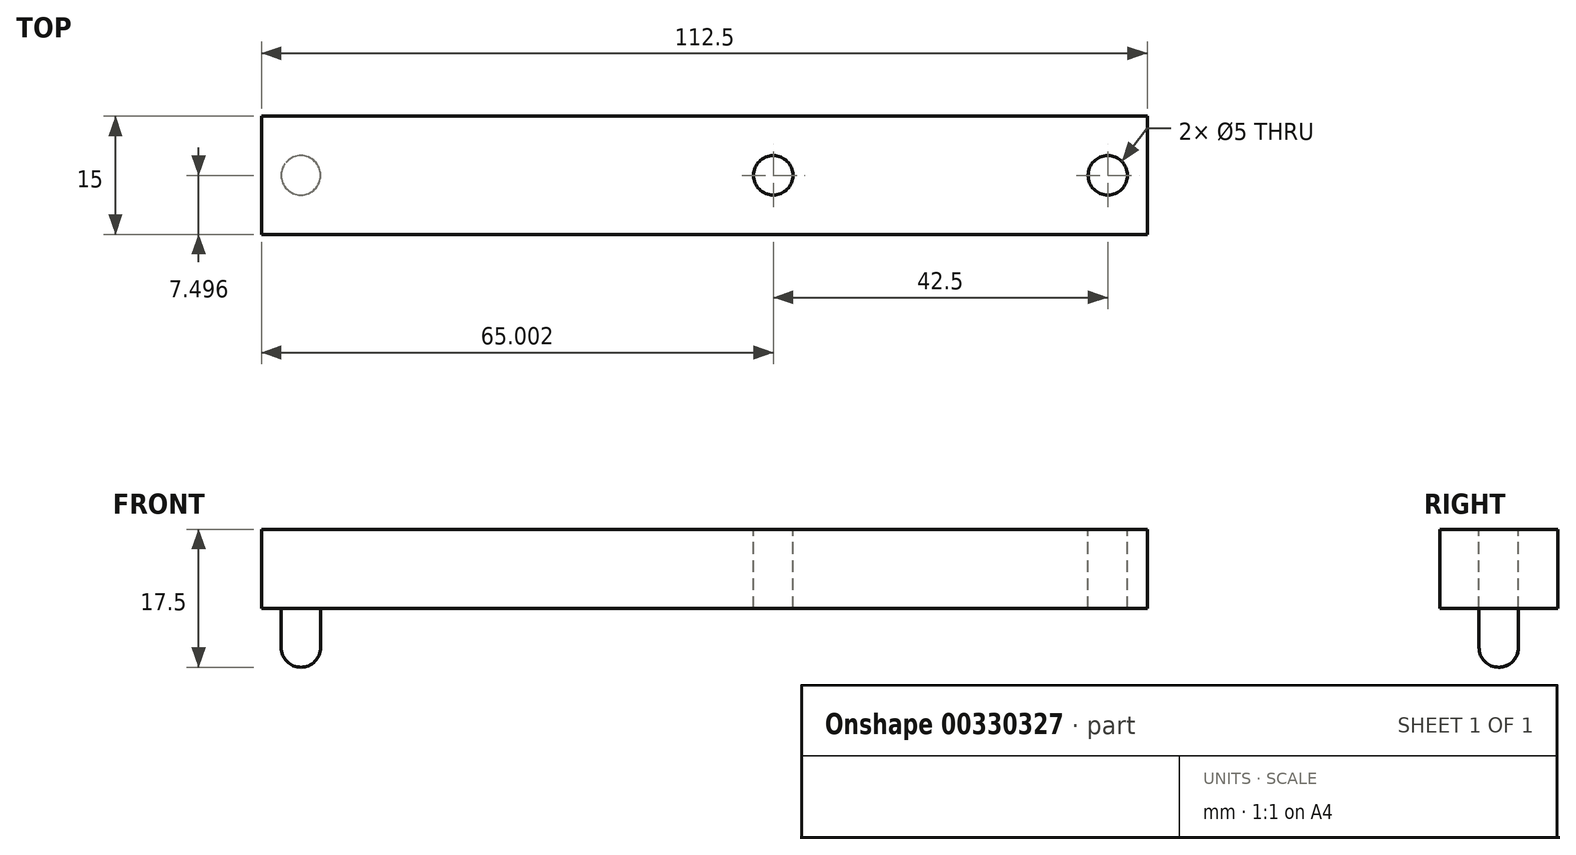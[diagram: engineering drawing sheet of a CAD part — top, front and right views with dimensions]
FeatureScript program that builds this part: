
annotation { "Feature Type Name" : "Feature", "Feature Type Description" : "" }
export const myFeature = defineFeature(function(context is Context, id is Id, definition is map)
    precondition{}
    {
        {
            var Q0;
            Q0=qCreatedBy(makeId("Top.planeOp"),FACE);
            var sketch = newSketch(context, id + "F0", { "sketchPlane" : qUnion([Q0])});
            skLineSegment(sketch, "E0.bottom", {"start": v(-62.77, 14.07) * mm, "end": v(-10.27, 14.07) * mm});
            skLineSegment(sketch, "E0.top", {"start": v(-62.77, -0.93) * mm, "end": v(-10.27, -0.93) * mm});
            skLineSegment(sketch, "E0.left", {"start": v(-62.77, 14.07) * mm, "end": v(-62.77, -0.93) * mm});
            skLineSegment(sketch, "E0.right", {"start": v(-10.27, 14.07) * mm, "end": v(-10.27, -0.93) * mm});
            skSolve(sketch);
        }
        {
            var Q0;
            Q0=makeQuery(id+"F0.imprint","IMPRINT",FACE,{"disambiguationData":[TD([[makeQuery(id+"F0.imprint","IMPRINT",EDGE,{"derivedFrom":sQuery(id+"F0.wireOp",EDGE,"E0.bottom")}),-1.0]])]});
            extrude(context, id + "F1", {"entities" : qUnion([Q0]), "depth" : 10 * mm});
        }
        {
            var Q0;
            Q0=makeQuery(id+"F1.opExtrude","CAP_FACE",FACE,{"disambiguationData":[OSD([sQuery(id+"F0.wireOp",EDGE,"E0.bottom"),sQuery(id+"F0.wireOp",EDGE,"E0.top"),sQuery(id+"F0.wireOp",EDGE,"E0.left"),sQuery(id+"F0.wireOp",EDGE,"E0.right")])],"isStart":false});
            var sketch = newSketch(context, id + "F2", { "sketchPlane" : qUnion([Q0])});
            skLineSegment(sketch, "E1", {"start": v(-62.77, 6.57) * mm, "end": v(-10.27, 6.57) * mm, "construction": true});
            skLineSegment(sketch, "E2", {"start": v(-15.27, 14.07) * mm, "end": v(-15.27, -0.93) * mm, "construction": true});
            skLineSegment(sketch, "E3", {"start": v(-57.77, -0.93) * mm, "end": v(-57.77, 14.07) * mm, "construction": true});
            skCircle(sketch, "E4", {"center": v(-57.77, 6.57) * mm, "radius": 2.5 * mm});
            skCircle(sketch, "E5", {"center": v(-15.27, 6.57) * mm, "radius": 2.5 * mm});
            skSolve(sketch);
        }
        {
            var Q0;
            Q0=makeQuery(id+"F2.imprint","IMPRINT",FACE,{"disambiguationData":[TD([[makeQuery(id+"F2.imprint","IMPRINT",EDGE,{"derivedFrom":sQuery(id+"F2.wireOp",EDGE,"E5")}),1.0]])]});
            var Q1;
            Q1=makeQuery(id+"F2.imprint","IMPRINT",FACE,{"disambiguationData":[TD([[makeQuery(id+"F2.imprint","IMPRINT",EDGE,{"derivedFrom":sQuery(id+"F2.wireOp",EDGE,"E4")}),1.0]])]});
            extrude(context, id + "F3", {"entities" : qUnion([Q0, Q1]), "operationType" : NewBodyOperationType.REMOVE, "oppositeDirection" : true, "depth" : 25 * mm});
        }
        {
            var Q0;
            Q0=makeQuery(id+"F1.opExtrude","SWEPT_FACE",FACE,{"disambiguationData":[OSD([sQuery(id+"F0.wireOp",EDGE,"E0.left")])]});
            var sketch = newSketch(context, id + "F4", { "sketchPlane" : qUnion([Q0])});
            skLineSegment(sketch, "E6.bottom", {"start": v(0.93, 10) * mm, "end": v(-14.07, 10) * mm});
            skLineSegment(sketch, "E6.top", {"start": v(0.93, 0) * mm, "end": v(-14.07, 0) * mm});
            skLineSegment(sketch, "E6.left", {"start": v(0.93, 10) * mm, "end": v(0.93, 0) * mm});
            skLineSegment(sketch, "E6.right", {"start": v(-14.07, 10) * mm, "end": v(-14.07, 0) * mm});
            skSolve(sketch);
        }
        {
            var Q0;
            Q0 = qSketchRegion(id + "F4", true);
            extrude(context, id + "F5", {"entities" : qUnion([Q0]), "operationType" : NewBodyOperationType.ADD, "depth" : 60 * mm});
        }
        {
            var Q0;
            Q0=makeQuery(id+"F5.boolean.opBoolean","MERGE",FACE,{"derivedFrom":[makeQuery(id+"F1.opExtrude","CAP_FACE",FACE,{"disambiguationData":[OSD([sQuery(id+"F0.wireOp",EDGE,"E0.bottom"),sQuery(id+"F0.wireOp",EDGE,"E0.top"),sQuery(id+"F0.wireOp",EDGE,"E0.left"),sQuery(id+"F0.wireOp",EDGE,"E0.right")])],"isStart":true}),makeQuery(id+"F5.opExtrude","SWEPT_FACE",FACE,{"disambiguationData":[OSD([sQuery(id+"F4.wireOp",EDGE,"E6.top")])]})]});
            var sketch = newSketch(context, id + "F6", { "sketchPlane" : qUnion([Q0])});
            skLineSegment(sketch, "E7", {"start": v(-122.77, -6.57) * mm, "end": v(-117.77, -6.57) * mm, "construction": true});
            skCircle(sketch, "E8", {"center": v(-117.77, -6.57) * mm, "radius": 2.5 * mm});
            skLineSegment(sketch, "E9", {"start": v(-117.77, -9.07) * mm, "end": v(-117.77, -4.07) * mm, "construction": true});
            skSolve(sketch);
        }
        {
            var Q0;
            Q0 = qSketchRegion(id + "F6", true);
            extrude(context, id + "F7", {"entities" : qUnion([Q0]), "operationType" : NewBodyOperationType.ADD, "depth" : 5 * mm});
        }
        {
            var Q0;
            Q0=makeQuery(id+"F5.opExtrude","CAP_FACE",FACE,{"disambiguationData":[OSD([sQuery(id+"F4.wireOp",EDGE,"E6.bottom"),sQuery(id+"F4.wireOp",EDGE,"E6.top"),sQuery(id+"F4.wireOp",EDGE,"E6.left"),sQuery(id+"F4.wireOp",EDGE,"E6.right")])],"isStart":false});
            cPlane(context, id + "F8", {"entities" : qUnion([Q0]), "cplaneType" : CPlaneType.OFFSET, "offset" : 5 * mm, "oppositeDirection" : true, "width" : 150 * mm, "height" : 150 * mm});
        }
        {
            var Q0;
            Q0=makeQuery(id+"F7.opExtrude","CAP_FACE",FACE,{"disambiguationData":[OSD([sQuery(id+"F6.wireOp",EDGE,"E8")])],"isStart":false});
            var sketch = newSketch(context, id + "F9", { "sketchPlane" : qUnion([Q0])});
            skLineSegment(sketch, "E10", {"start": v(-117.77, -6.57) * mm, "end": v(-117.77, -4.07) * mm, "construction": true});
            skLineSegment(sketch, "E11", {"start": v(-117.77, -4.07) * mm, "end": v(-117.77, -9.07) * mm, "construction": true});
            skSolve(sketch);
        }
        {
            var Q0;
            Q0=qCreatedBy(id+"F8.planeOp",FACE);
            var sketch = newSketch(context, id + "F10", { "sketchPlane" : qUnion([Q0])});
            skLineSegment(sketch, "E12", {"start": v(-9.07, -5) * mm, "end": v(-6.57, -5) * mm});
            skLineSegment(sketch, "E13", {"start": v(-6.57, -5) * mm, "end": v(-6.57, -7.5) * mm});
            skArc(sketch, "E14", {"start": v(-9.07, -5) * mm, "mid": v(-8.33, -6.77) * mm, "end": v(-6.57, -7.5) * mm});
            skSolve(sketch);
        }
        {
            var Q0;
            Q0=makeQuery(id+"F10.imprint","IMPRINT",FACE,{"disambiguationData":[TD([[makeQuery(id+"F10.imprint","IMPRINT",EDGE,{"derivedFrom":sQuery(id+"F10.wireOp",EDGE,"E12")}),-1.0]])]});
            var Q1;
            Q1=sQuery(id+"F10.wireOp",EDGE,"E14");
            var Q2;
            Q2=sQuery(id+"F10.wireOp",EDGE,"E13");
            var Q3;
            Q3=sQuery(id+"F10.wireOp",EDGE,"E12");
            var Q4;
            Q4=sQuery(id+"F10.wireOp",EDGE,"E13");
            revolve(context, id + "F11", {"operationType" : NewBodyOperationType.ADD, "entities" : qUnion([Q0]), "surfaceEntities" : qUnion([Q1, Q2, Q3]), "axis" : qUnion([Q4]), "revolveType" : RevolveType.FULL});
        }
    });
